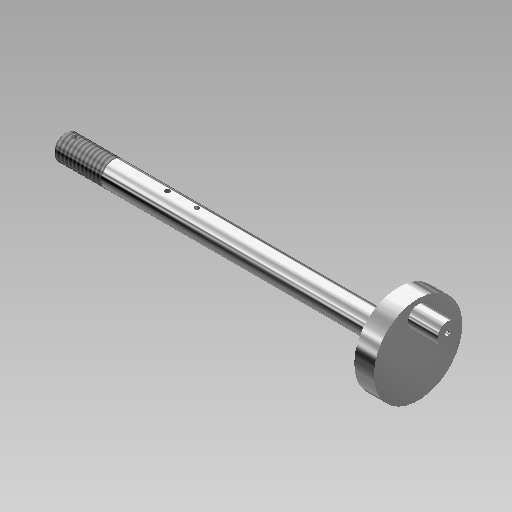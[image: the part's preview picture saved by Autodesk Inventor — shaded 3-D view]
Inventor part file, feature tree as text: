
AUTODESK INVENTOR PART (.ipt)
format: ipt  version: 2018.1 (Build 221171000, 171)  size: 142,848 bytes
history: native  units: in
note: dims shown in document units (in); Inventor stores cm internally (conversion verified against a paired STEP export)
features: sketch x5, extrude x4, revolve x1, chamfer x1, thread x1
ambient origin geometry x8: Origin, YZ Plane, XZ Plane, XY Plane, X Axis, Y Axis, Z Axis, Center Point
bodies: Solid1 (feature_tree)
feature tree (12):
  revolve  "Revolution1"  Angle=45.0deg
  chamfer  "Chamfer1"  Distance=0.3937in
  thread  "Thread1"  [1 undecoded]
  extrude  "Extrusion1"  Depth=0.3937in TaperAngle=0.0deg
  extrude  "Extrusion2"  [1 undecoded]
  extrude  "Extrusion3"  [1 undecoded]
  extrude  "Extrusion4"  [1 undecoded]
  sketch  "Sketch1"  dims[d4=90.0deg d5=0.0197in d6=0.0787in d7=45.0deg d8=0.3937in d9=2.2835in d13=0.2362in d14=0.0in]
  sketch  "Sketch2"  dims[d17=0.3937in d18=0.0in d22=0.3937in d23=0.0in]
  sketch  "Sketch3"  dims[d26=0.3937in d27=0.0in]
  sketch  "Sketch4"
  sketch  "Sketch5"
note: 4 required parameter values undecoded (feature->parameter linkage not recoverable at this tier; creation-order binding heuristic only, values carry confidence <= 0.55)
